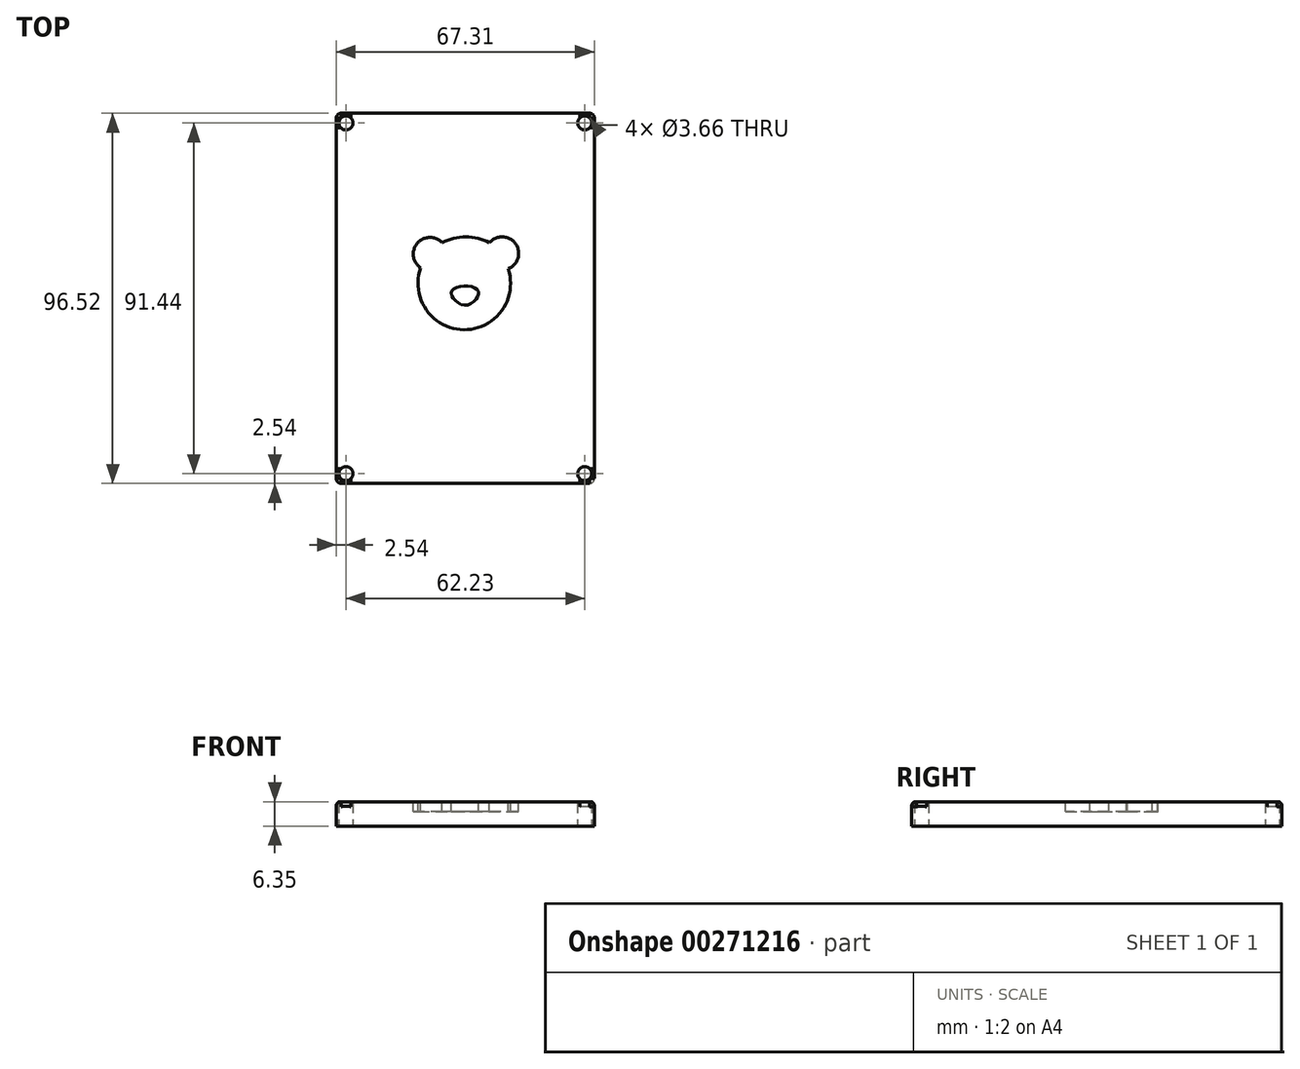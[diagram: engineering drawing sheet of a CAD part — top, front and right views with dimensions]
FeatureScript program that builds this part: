
annotation { "Feature Type Name" : "Feature", "Feature Type Description" : "" }
export const myFeature = defineFeature(function(context is Context, id is Id, definition is map)
    precondition{}
    {
        {
            var Q0;
            Q0=qCreatedBy(makeId("Top.planeOp"),FACE);
            var sketch = newSketch(context, id + "F0", { "sketchPlane" : qUnion([Q0])});
            skLineSegment(sketch, "E0.bottom", {"start": v(1.27, 0) * mm, "end": v(66.04, 0) * mm});
            skLineSegment(sketch, "E0.top", {"start": v(1.27, 96.52) * mm, "end": v(66.04, 96.52) * mm});
            skLineSegment(sketch, "E0.left", {"start": v(0, 1.27) * mm, "end": v(0, 95.25) * mm});
            skLineSegment(sketch, "E0.right", {"start": v(67.31, 1.27) * mm, "end": v(67.3, 95.25) * mm});
            skPoint(sketch, "E1.visualSharp", {"position": v(0, 96.52) * mm});
            skArc(sketch, "E1.filletArc", {"start": v(1.27, 96.52) * mm, "mid": v(0.37, 96.15) * mm, "end": v(0, 95.25) * mm});
            skPoint(sketch, "E2.visualSharp", {"position": v(67.3, 96.52) * mm});
            skArc(sketch, "E2.filletArc", {"start": v(67.3, 95.25) * mm, "mid": v(66.94, 96.15) * mm, "end": v(66.04, 96.52) * mm});
            skPoint(sketch, "E3.visualSharp", {"position": v(67.31, 0) * mm});
            skArc(sketch, "E3.filletArc", {"start": v(66.04, 0) * mm, "mid": v(66.94, 0.37) * mm, "end": v(67.31, 1.27) * mm});
            skPoint(sketch, "E4.visualSharp", {"position": v(0, 0) * mm});
            skArc(sketch, "E4.filletArc", {"start": v(0, 1.27) * mm, "mid": v(0.37, 0.37) * mm, "end": v(1.27, 0) * mm});
            skLineSegment(sketch, "E5.bottom", {"start": v(2.54, 93.98) * mm, "end": v(64.77, 93.98) * mm, "construction": true});
            skLineSegment(sketch, "E5.top", {"start": v(2.54, 2.54) * mm, "end": v(64.77, 2.54) * mm, "construction": true});
            skLineSegment(sketch, "E5.left", {"start": v(2.54, 93.98) * mm, "end": v(2.54, 2.54) * mm, "construction": true});
            skLineSegment(sketch, "E5.right", {"start": v(64.77, 93.98) * mm, "end": v(64.77, 2.54) * mm, "construction": true});
            skCircle(sketch, "E6", {"center": v(2.54, 93.98) * mm, "radius": 1.83 * mm});
            skCircle(sketch, "E7", {"center": v(64.77, 2.54) * mm, "radius": 1.83 * mm});
            skCircle(sketch, "E8", {"center": v(2.54, 2.54) * mm, "radius": 1.83 * mm});
            skCircle(sketch, "E9", {"center": v(64.77, 93.98) * mm, "radius": 1.83 * mm});
            skSolve(sketch);
        }
        {
            var Q0;
            Q0 = qSketchRegion(id + "F0", true);
            extrude(context, id + "F1", {"entities" : qUnion([Q0]), "depth" : 6.35 * mm});
        }
        {
            var Q0;
            Q0=makeQuery(id+"F1.opExtrude","CAP_EDGE",EDGE,{"disambiguationData":[OSD([sQuery(id+"F0.wireOp",EDGE,"E0.right")])],"isStart":false});
            var Q1;
            Q1=makeQuery(id+"F1.opExtrude","CAP_EDGE",EDGE,{"disambiguationData":[OSD([sQuery(id+"F0.wireOp",EDGE,"E0.bottom")])],"isStart":false});
            var Q2;
            Q2=makeQuery(id+"F1.opExtrude","CAP_EDGE",EDGE,{"disambiguationData":[OSD([sQuery(id+"F0.wireOp",EDGE,"E0.left")])],"isStart":false});
            var Q3;
            Q3=makeQuery(id+"F1.opExtrude","CAP_EDGE",EDGE,{"disambiguationData":[OSD([sQuery(id+"F0.wireOp",EDGE,"E0.top")])],"isStart":false});
            fillet(context, id + "F2", {"entities" : qUnion([Q0, Q1, Q2, Q3]), "radius" : 1.27 * mm, "tangentPropagation" : true, "allowEdgeOverflow" : false});
        }
        {
            var Q0;
            Q0=makeQuery(id+"F1.opExtrude","CAP_FACE",FACE,{"disambiguationData":[OSD([sQuery(id+"F0.wireOp",EDGE,"E0.bottom"),sQuery(id+"F0.wireOp",EDGE,"E0.top"),sQuery(id+"F0.wireOp",EDGE,"E0.left"),sQuery(id+"F0.wireOp",EDGE,"E0.right"),sQuery(id+"F0.wireOp",EDGE,"E1.filletArc"),sQuery(id+"F0.wireOp",EDGE,"E2.filletArc"),sQuery(id+"F0.wireOp",EDGE,"E3.filletArc"),sQuery(id+"F0.wireOp",EDGE,"E4.filletArc"),sQuery(id+"F0.wireOp",EDGE,"E6"),sQuery(id+"F0.wireOp",EDGE,"E7"),sQuery(id+"F0.wireOp",EDGE,"E8"),sQuery(id+"F0.wireOp",EDGE,"E9")])],"isStart":false});
            var sketch = newSketch(context, id + "F3", { "sketchPlane" : qUnion([Q0])});
            skArc(sketch, "E10", {"start": v(22.03, 56.2) * mm, "mid": v(33.26, 40.07) * mm, "end": v(44.83, 55.96) * mm});
            skArc(sketch, "E11", {"start": v(44.83, 55.96) * mm, "mid": v(46.74, 62.5) * mm, "end": v(39.94, 62.7) * mm});
            skArc(sketch, "E12", {"start": v(27.62, 62.74) * mm, "mid": v(21.14, 62.61) * mm, "end": v(22.03, 56.2) * mm});
            skArc(sketch, "E13", {"start": v(39.94, 62.7) * mm, "mid": v(33.78, 64.3) * mm, "end": v(27.62, 62.74) * mm});
            skFitSpline(sketch, "E14", {"points": [v(30.16, 50.22) * mm, v(36.94, 50.36) * mm, v(33.76, 46.48) * mm, v(30.16, 50.22) * mm]});
            skSolve(sketch);
        }
        {
            var Q0;
            Q0 = qSketchRegion(id + "F3", true);
            extrude(context, id + "F4", {"entities" : qUnion([Q0]), "operationType" : NewBodyOperationType.REMOVE, "oppositeDirection" : true, "depth" : 2.54 * mm});
        }
    });
